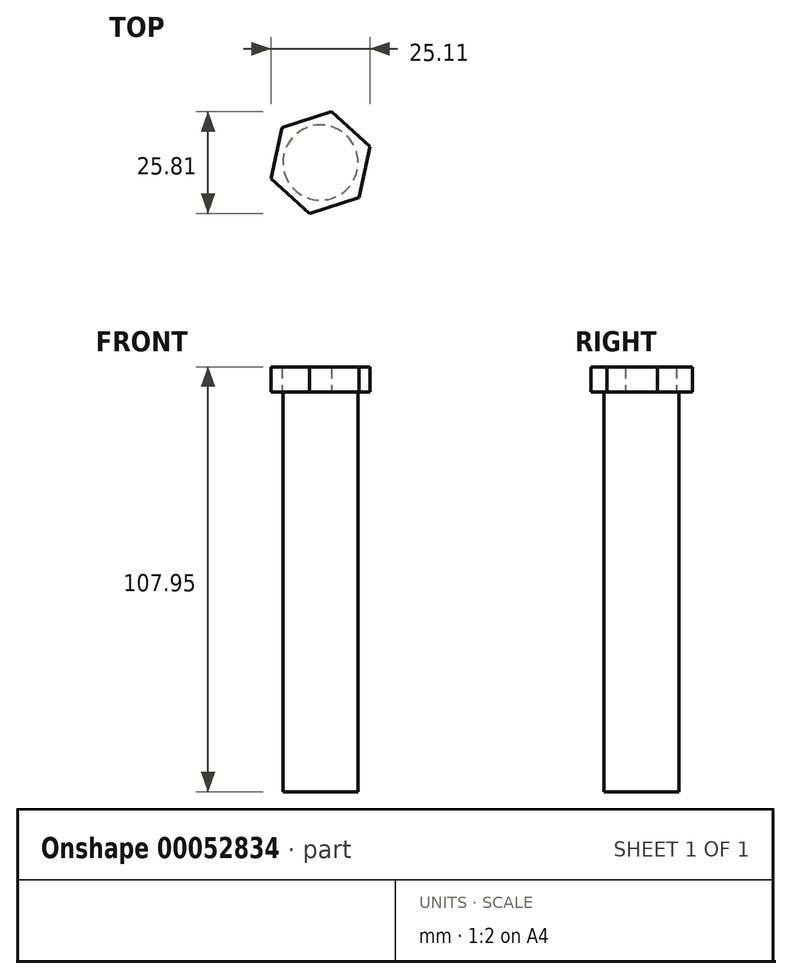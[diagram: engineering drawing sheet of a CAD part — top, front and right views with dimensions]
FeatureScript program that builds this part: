
annotation { "Feature Type Name" : "Feature", "Feature Type Description" : "" }
export const myFeature = defineFeature(function(context is Context, id is Id, definition is map)
    precondition{}
    {
        {
            var Q0;
            Q0=qCreatedBy(makeId("Top.planeOp"),FACE);
            var sketch = newSketch(context, id + "F0", { "sketchPlane" : qUnion([Q0])});
            skCircle(sketch, "E0.cCircle", {"center": v(-25.07, 3.87) * mm, "radius": 11.43 * mm, "construction": true});
            skLineSegment(sketch, "E0.0", {"start": v(-34.87, 12.72) * mm, "end": v(-22.3, 16.78) * mm});
            skLineSegment(sketch, "E0.1", {"start": v(-22.3, 16.78) * mm, "end": v(-12.52, 7.93) * mm});
            skLineSegment(sketch, "E0.2", {"start": v(-12.52, 7.93) * mm, "end": v(-15.28, -4.97) * mm});
            skLineSegment(sketch, "E0.3", {"start": v(-15.28, -4.97) * mm, "end": v(-27.84, -9.03) * mm});
            skLineSegment(sketch, "E0.4", {"start": v(-27.84, -9.03) * mm, "end": v(-37.63, -0.18) * mm});
            skLineSegment(sketch, "E0.5", {"start": v(-37.63, -0.18) * mm, "end": v(-34.87, 12.72) * mm});
            skPoint(sketch, "E0.0.midPoint", {"position": v(-28.59, 14.75) * mm});
            skSolve(sketch);
        }
        {
            var Q0;
            Q0 = qSketchRegion(id + "F0", true);
            extrude(context, id + "F1", {"entities" : qUnion([Q0]), "depth" : 6.35 * mm});
        }
        {
            var Q0;
            Q0=makeQuery(id+"F1.opExtrude","CAP_FACE",FACE,{"disambiguationData":[OSD([sQuery(id+"F0.wireOp",EDGE,"E0.0"),sQuery(id+"F0.wireOp",EDGE,"E0.1"),sQuery(id+"F0.wireOp",EDGE,"E0.2"),sQuery(id+"F0.wireOp",EDGE,"E0.3"),sQuery(id+"F0.wireOp",EDGE,"E0.4"),sQuery(id+"F0.wireOp",EDGE,"E0.5")])],"isStart":true});
            var sketch = newSketch(context, id + "F2", { "sketchPlane" : qUnion([Q0])});
            skLineSegment(sketch, "E1", {"start": v(-27.84, 9.03) * mm, "end": v(-22.3, -16.78) * mm, "construction": true});
            skCircle(sketch, "E2", {"center": v(-25.07, -3.87) * mm, "radius": 9.53 * mm});
            skSolve(sketch);
        }
        {
            var Q0;
            Q0 = qSketchRegion(id + "F2", true);
            extrude(context, id + "F3", {"entities" : qUnion([Q0]), "operationType" : NewBodyOperationType.ADD, "depth" : 101.6 * mm});
        }
    });
